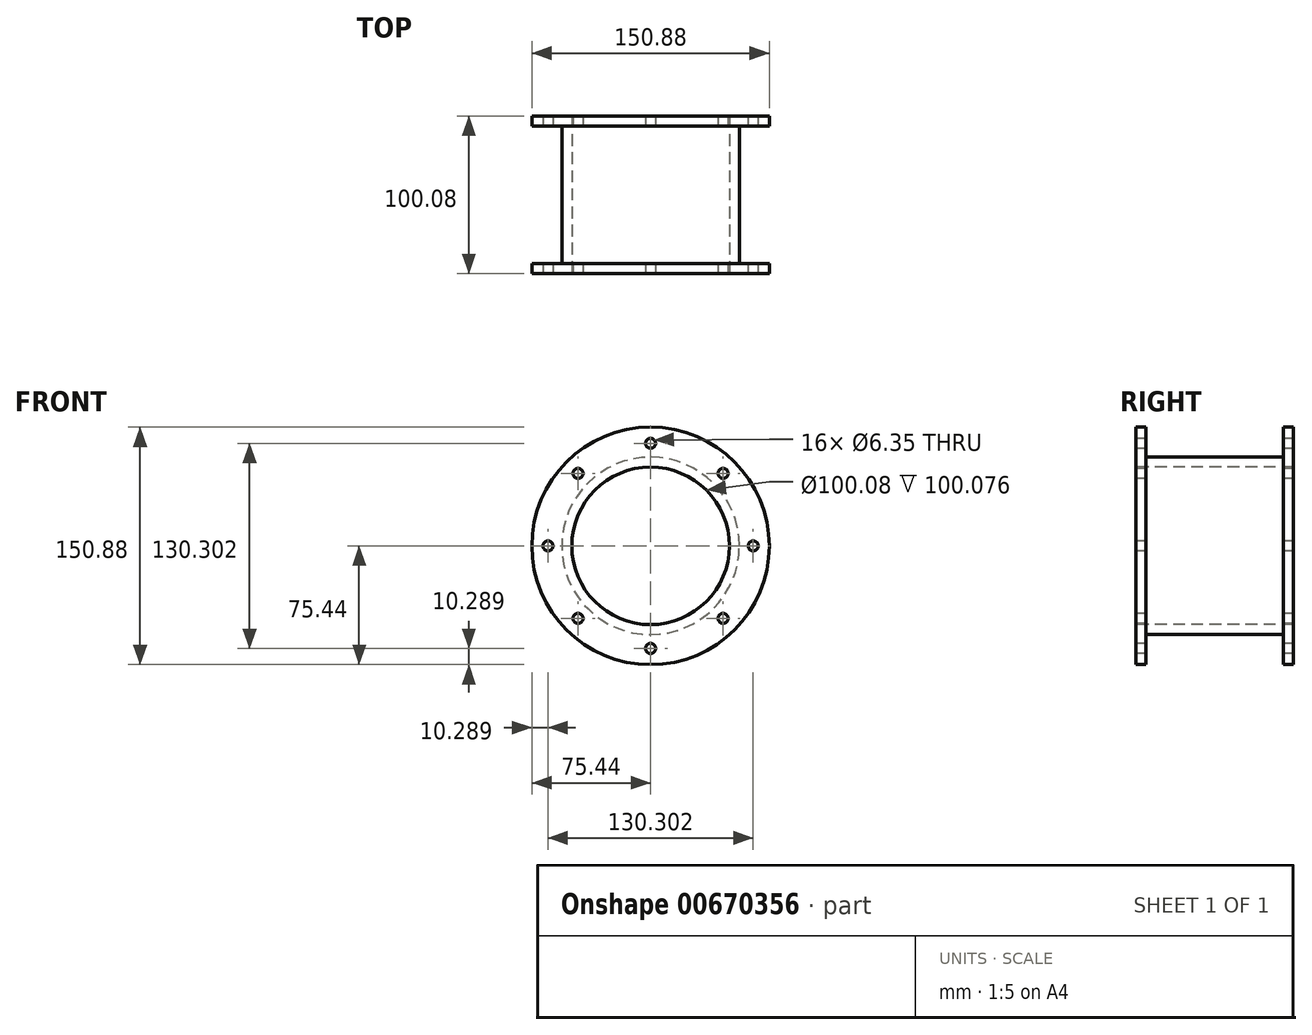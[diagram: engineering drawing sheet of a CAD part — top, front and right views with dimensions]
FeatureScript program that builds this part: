
annotation { "Feature Type Name" : "Feature", "Feature Type Description" : "" }
export const myFeature = defineFeature(function(context is Context, id is Id, definition is map)
    precondition{}
    {
        {
            var Q0;
            Q0=qCreatedBy(makeId("Right.planeOp"),FACE);
            var sketch = newSketch(context, id + "F0", { "sketchPlane" : qUnion([Q0])});
            skLineSegment(sketch, "E0", {"start": v(0, 0) * mm, "end": v(108.18, 0) * mm, "construction": true});
            skLineSegment(sketch, "E1.bottom", {"start": v(0, 50.04) * mm, "end": v(100.08, 50.04) * mm});
            skLineSegment(sketch, "E1.top", {"start": v(0, 56.39) * mm, "end": v(100.08, 56.39) * mm});
            skLineSegment(sketch, "E1.left", {"start": v(0, 50.04) * mm, "end": v(0, 56.39) * mm});
            skLineSegment(sketch, "E1.right", {"start": v(100.08, 50.04) * mm, "end": v(100.08, 56.39) * mm});
            skLineSegment(sketch, "E2.bottom", {"start": v(0, 50.04) * mm, "end": v(6.35, 50.04) * mm});
            skLineSegment(sketch, "E2.top", {"start": v(0, 75.44) * mm, "end": v(6.35, 75.44) * mm});
            skLineSegment(sketch, "E2.left", {"start": v(0, 50.04) * mm, "end": v(0, 75.44) * mm});
            skLineSegment(sketch, "E2.right", {"start": v(6.35, 50.04) * mm, "end": v(6.35, 75.44) * mm});
            skLineSegment(sketch, "E3.bottom", {"start": v(100.08, 50.04) * mm, "end": v(93.73, 50.04) * mm});
            skLineSegment(sketch, "E3.top", {"start": v(100.08, 75.44) * mm, "end": v(93.73, 75.44) * mm});
            skLineSegment(sketch, "E3.left", {"start": v(100.08, 50.04) * mm, "end": v(100.08, 75.44) * mm});
            skLineSegment(sketch, "E3.right", {"start": v(93.73, 50.04) * mm, "end": v(93.73, 75.44) * mm});
            skLineSegment(sketch, "E4.MirrorCS", {"start": v(100.08, -75.44) * mm, "end": v(93.73, -75.44) * mm});
            skLineSegment(sketch, "E5.MirrorCS", {"start": v(100.08, -50.04) * mm, "end": v(93.73, -50.04) * mm});
            skLineSegment(sketch, "E6.MirrorCS", {"start": v(0, -75.44) * mm, "end": v(6.35, -75.44) * mm});
            skLineSegment(sketch, "E7.MirrorCS", {"start": v(0, -50.04) * mm, "end": v(6.35, -50.04) * mm});
            skLineSegment(sketch, "E8.MirrorCS", {"start": v(100.08, -50.04) * mm, "end": v(100.08, -56.39) * mm});
            skLineSegment(sketch, "E9.MirrorCS", {"start": v(0, -50.04) * mm, "end": v(0, -56.39) * mm});
            skLineSegment(sketch, "E10.MirrorCS", {"start": v(93.73, -50.04) * mm, "end": v(93.73, -75.44) * mm});
            skLineSegment(sketch, "E11.MirrorCS", {"start": v(100.08, -50.04) * mm, "end": v(100.08, -75.44) * mm});
            skLineSegment(sketch, "E12.MirrorCS", {"start": v(6.35, -50.04) * mm, "end": v(6.35, -75.44) * mm});
            skLineSegment(sketch, "E13.MirrorCS", {"start": v(0, -50.04) * mm, "end": v(0, -75.44) * mm});
            skLineSegment(sketch, "E14.MirrorCS", {"start": v(0, -50.04) * mm, "end": v(100.08, -50.04) * mm});
            skLineSegment(sketch, "E15.MirrorCS", {"start": v(0, -56.39) * mm, "end": v(100.08, -56.39) * mm});
            skSolve(sketch);
        }
        {
            var Q0;
            {var subQ5=sQuery(id+"F0.wireOp",EDGE,"E2.top");Q0=makeQuery(id+"F0.imprint","IMPRINT",FACE,{"disambiguationData":[TD([[makeQuery(id+"F0.imprint","IMPRINT",EDGE,{"derivedFrom":subQ5}),-1.0]])]});}
            var Q1;
            {var subQ5=sQuery(id+"F0.wireOp",EDGE,"E3.top");Q1=makeQuery(id+"F0.imprint","IMPRINT",FACE,{"disambiguationData":[TD([[makeQuery(id+"F0.imprint","IMPRINT",EDGE,{"derivedFrom":subQ5}),1.0]])]});}
            var Q2;
            {var subQ0=sQuery(id+"F0.wireOp",EDGE,"E1.bottom");Q2=makeQuery(id+"F0.imprint","IMPRINT",FACE,{"disambiguationData":[TD([[makeQuery(id+"F0.imprint","IMPRINT",EDGE,{"derivedFrom":subQ0}),1.0]])]});}
            var Q3;
            {var subQ5=sQuery(id+"F0.wireOp",EDGE,"E2.bottom");Q3=makeQuery(id+"F0.imprint","IMPRINT",FACE,{"disambiguationData":[TD([[makeQuery(id+"F0.imprint","IMPRINT",EDGE,{"derivedFrom":subQ5}),1.0]])]});}
            var Q4;
            {var subQ5=sQuery(id+"F0.wireOp",EDGE,"E3.bottom");Q4=makeQuery(id+"F0.imprint","IMPRINT",FACE,{"disambiguationData":[TD([[makeQuery(id+"F0.imprint","IMPRINT",EDGE,{"derivedFrom":subQ5}),-1.0]])]});}
            var Q5;
            Q5=sQuery(id+"F0.wireOp",EDGE,"E0");
            revolve(context, id + "F1", {"entities" : qUnion([Q0, Q1, Q2, Q3, Q4]), "axis" : qUnion([Q5]), "revolveType" : RevolveType.FULL});
        }
        {
            var Q0;
            Q0=makeQuery(id+"F1.opRevolve","SWEPT_FACE",FACE,{"disambiguationData":[OSD([sQuery(id+"F0.wireOp",EDGE,"E2.left")])]});
            var sketch = newSketch(context, id + "F2", { "sketchPlane" : qUnion([Q0])});
            skLineSegment(sketch, "E16", {"start": v(0, 0) * mm, "end": v(0, 65.15) * mm, "construction": true});
            skLineSegment(sketch, "E17", {"start": v(0, 0) * mm, "end": v(0, -65.15) * mm, "construction": true});
            skLineSegment(sketch, "E18", {"start": v(0, 0) * mm, "end": v(-65.15, 0) * mm, "construction": true});
            skLineSegment(sketch, "E19", {"start": v(0, 0) * mm, "end": v(65.15, 0) * mm, "construction": true});
            skLineSegment(sketch, "E20", {"start": v(0, 0) * mm, "end": v(46.07, 46.07) * mm, "construction": true});
            skLineSegment(sketch, "E21", {"start": v(0, 0) * mm, "end": v(-46.07, 46.07) * mm, "construction": true});
            skLineSegment(sketch, "E22", {"start": v(0, 0) * mm, "end": v(-46.07, -46.07) * mm, "construction": true});
            skLineSegment(sketch, "E23", {"start": v(0, 0) * mm, "end": v(46.07, -46.07) * mm, "construction": true});
            skCircle(sketch, "E24", {"center": v(-46.07, 46.07) * mm, "radius": 3.18 * mm});
            skCircle(sketch, "E25", {"center": v(-65.15, 0) * mm, "radius": 3.18 * mm});
            skCircle(sketch, "E26", {"center": v(-46.07, -46.07) * mm, "radius": 3.18 * mm});
            skCircle(sketch, "E27", {"center": v(0, -65.15) * mm, "radius": 3.18 * mm});
            skCircle(sketch, "E28", {"center": v(46.07, -46.07) * mm, "radius": 3.18 * mm});
            skCircle(sketch, "E29", {"center": v(65.15, 0) * mm, "radius": 3.18 * mm});
            skCircle(sketch, "E30", {"center": v(46.07, 46.07) * mm, "radius": 3.18 * mm});
            skCircle(sketch, "E31", {"center": v(0, 65.15) * mm, "radius": 3.17 * mm});
            skSolve(sketch);
        }
        {
            var Q0;
            Q0=makeQuery(id+"F2.imprint","IMPRINT",FACE,{"disambiguationData":[TD([[makeQuery(id+"F2.imprint","IMPRINT",EDGE,{"derivedFrom":sQuery(id+"F2.wireOp",EDGE,"E24")}),1.0]])]});
            var Q1;
            Q1=makeQuery(id+"F2.imprint","IMPRINT",FACE,{"disambiguationData":[TD([[makeQuery(id+"F2.imprint","IMPRINT",EDGE,{"derivedFrom":sQuery(id+"F2.wireOp",EDGE,"E25")}),1.0]])]});
            var Q2;
            Q2=makeQuery(id+"F2.imprint","IMPRINT",FACE,{"disambiguationData":[TD([[makeQuery(id+"F2.imprint","IMPRINT",EDGE,{"derivedFrom":sQuery(id+"F2.wireOp",EDGE,"E26")}),1.0]])]});
            var Q3;
            Q3=makeQuery(id+"F2.imprint","IMPRINT",FACE,{"disambiguationData":[TD([[makeQuery(id+"F2.imprint","IMPRINT",EDGE,{"derivedFrom":sQuery(id+"F2.wireOp",EDGE,"E27")}),1.0]])]});
            var Q4;
            Q4=makeQuery(id+"F2.imprint","IMPRINT",FACE,{"disambiguationData":[TD([[makeQuery(id+"F2.imprint","IMPRINT",EDGE,{"derivedFrom":sQuery(id+"F2.wireOp",EDGE,"E28")}),1.0]])]});
            var Q5;
            Q5=makeQuery(id+"F2.imprint","IMPRINT",FACE,{"disambiguationData":[TD([[makeQuery(id+"F2.imprint","IMPRINT",EDGE,{"derivedFrom":sQuery(id+"F2.wireOp",EDGE,"E29")}),1.0]])]});
            var Q6;
            Q6=makeQuery(id+"F2.imprint","IMPRINT",FACE,{"disambiguationData":[TD([[makeQuery(id+"F2.imprint","IMPRINT",EDGE,{"derivedFrom":sQuery(id+"F2.wireOp",EDGE,"E30")}),1.0]])]});
            var Q7;
            Q7=makeQuery(id+"F2.imprint","IMPRINT",FACE,{"disambiguationData":[TD([[makeQuery(id+"F2.imprint","IMPRINT",EDGE,{"derivedFrom":sQuery(id+"F2.wireOp",EDGE,"E31")}),1.0]])]});
            extrude(context, id + "F3", {"entities" : qUnion([Q0, Q1, Q2, Q3, Q4, Q5, Q6, Q7]), "operationType" : NewBodyOperationType.REMOVE, "endBound" : BoundingType.THROUGH_ALL, "oppositeDirection" : true, "depth" : 25.4 * mm, "offsetDistance" : 25.4 * mm});
        }
    });
